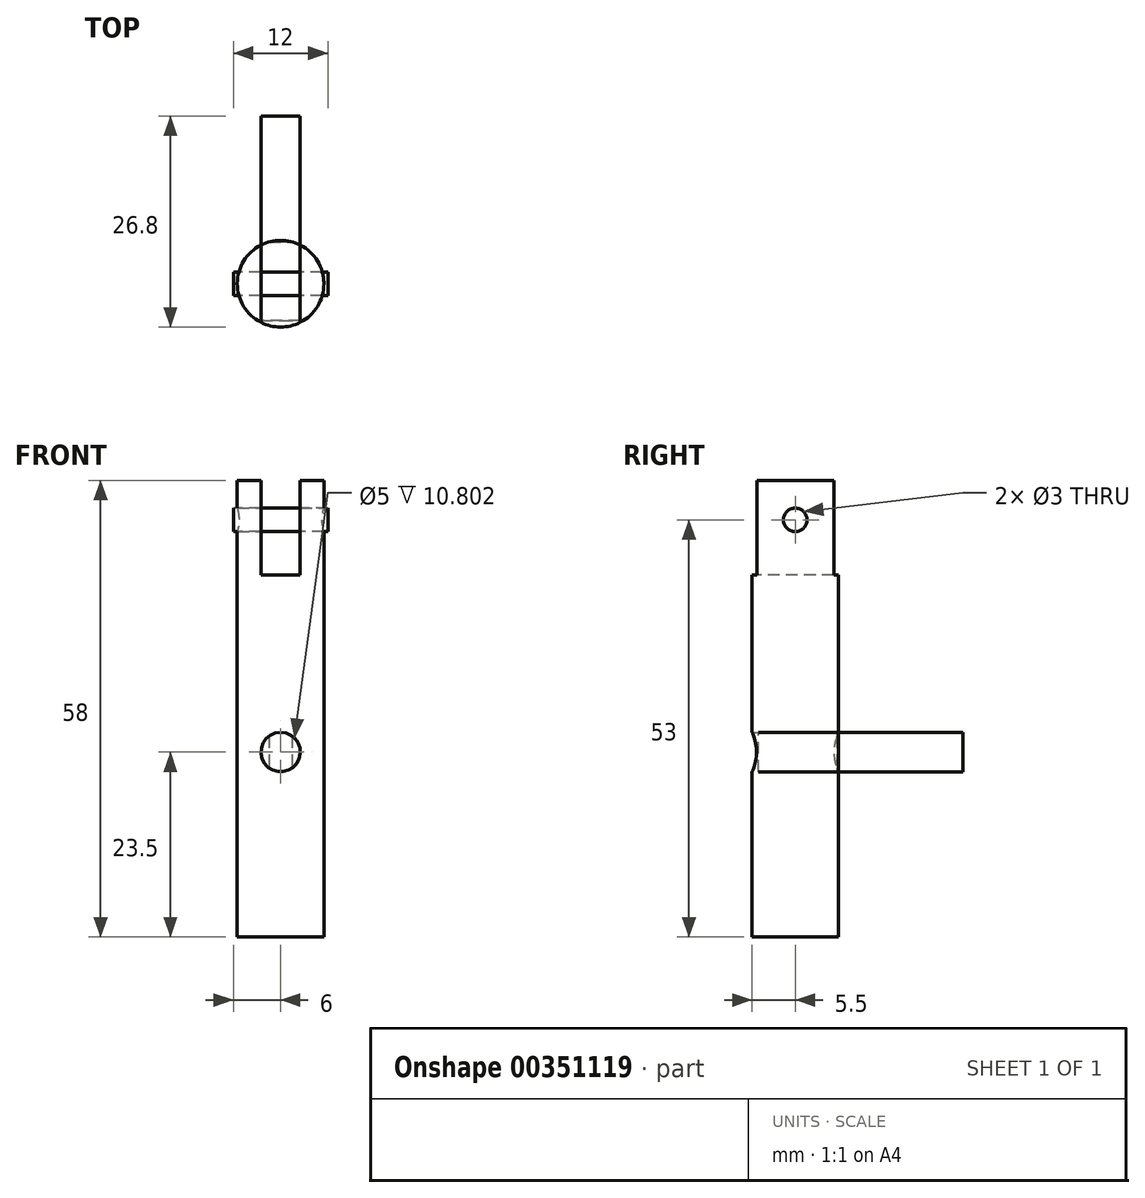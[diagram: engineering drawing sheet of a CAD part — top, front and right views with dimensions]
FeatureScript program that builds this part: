
annotation { "Feature Type Name" : "Feature", "Feature Type Description" : "" }
export const myFeature = defineFeature(function(context is Context, id is Id, definition is map)
    precondition{}
    {
        {
            var Q0;
            Q0=qCreatedBy(makeId("Top.planeOp"),FACE);
            var sketch = newSketch(context, id + "F0", { "sketchPlane" : qUnion([Q0])});
            skCircle(sketch, "E0", {"center": v(0, 0) * mm, "radius": 5.5 * mm});
            skSolve(sketch);
        }
        {
            var Q0;
            Q0=makeQuery(id+"F0.imprint","IMPRINT",FACE,{"disambiguationData":[TD([[makeQuery(id+"F0.imprint","IMPRINT",EDGE,{"derivedFrom":sQuery(id+"F0.wireOp",EDGE,"E0")}),1.0]])]});
            extrude(context, id + "F1", {"entities" : qUnion([Q0]), "depth" : 58 * mm});
        }
        {
            var Q0;
            Q0=makeQuery(id+"F1.opExtrude","CAP_FACE",FACE,{"disambiguationData":[OSD([sQuery(id+"F0.wireOp",EDGE,"E0")])],"isStart":false});
            var sketch = newSketch(context, id + "F2", { "sketchPlane" : qUnion([Q0])});
            skLineSegment(sketch, "E1", {"start": v(-2.5, 4.9) * mm, "end": v(-2.5, -4.9) * mm});
            skLineSegment(sketch, "E2", {"start": v(2.5, 4.9) * mm, "end": v(2.5, -4.9) * mm});
            skLineSegment(sketch, "E3", {"start": v(0, -1.95) * mm, "end": v(0, 2.72) * mm, "construction": true});
            skSolve(sketch);
        }
        {
            var Q0;
            {var subQ0=sQuery(id+"F2.wireOp",EDGE,"E1");Q0=makeQuery(id+"F2.imprint","IMPRINT",FACE,{"disambiguationData":[TD([[makeQuery(id+"F2.imprint","IMPRINT",EDGE,{"derivedFrom":subQ0}),1.0]])]});}
            extrude(context, id + "F3", {"entities" : qUnion([Q0]), "operationType" : NewBodyOperationType.REMOVE, "oppositeDirection" : true, "depth" : 12 * mm});
        }
        {
            var Q0;
            Q0=qCreatedBy(makeId("Right.planeOp"),FACE);
            cPlane(context, id + "F4", {"entities" : qUnion([Q0]), "cplaneType" : CPlaneType.OFFSET, "offset" : 5.5 * mm, "width" : 150 * mm, "height" : 150 * mm});
        }
        {
            var Q0;
            Q0=qCreatedBy(id+"F4.planeOp",FACE);
            var sketch = newSketch(context, id + "F5", { "sketchPlane" : qUnion([Q0])});
            skCircle(sketch, "E4", {"center": v(0, 53) * mm, "radius": 1.5 * mm});
            skSolve(sketch);
        }
        {
            var Q0;
            Q0=makeQuery(id+"F5.imprint","IMPRINT",FACE,{"disambiguationData":[TD([[makeQuery(id+"F5.imprint","IMPRINT",EDGE,{"derivedFrom":sQuery(id+"F5.wireOp",EDGE,"E4")}),1.0]])]});
            extrude(context, id + "F6", {"entities" : qUnion([Q0]), "operationType" : NewBodyOperationType.REMOVE, "endBound" : BoundingType.THROUGH_ALL, "oppositeDirection" : true, "depth" : 25 * mm});
        }
        {
            var Q0;
            Q0=makeQuery(id+"F5.imprint","IMPRINT",FACE,{"disambiguationData":[TD([[makeQuery(id+"F5.imprint","IMPRINT",EDGE,{"derivedFrom":sQuery(id+"F5.wireOp",EDGE,"E4")}),1.0]])]});
            extrude(context, id + "F7", {"entities" : qUnion([Q0]), "depth" : .5 * mm, "hasSecondDirection" : true, "secondDirectionOppositeDirection" : true, "secondDirectionDepth" : 11.5 * mm});
        }
        {
            var Q0;
            Q0=qCreatedBy(makeId("Front.planeOp"),FACE);
            cPlane(context, id + "F8", {"entities" : qUnion([Q0]), "cplaneType" : CPlaneType.OFFSET, "offset" : 5.3 * mm, "oppositeDirection" : true, "width" : 150 * mm, "height" : 150 * mm});
        }
        {
            var Q0;
            Q0=qCreatedBy(id+"F8.planeOp",FACE);
            var sketch = newSketch(context, id + "F9", { "sketchPlane" : qUnion([Q0])});
            skCircle(sketch, "E5", {"center": v(0, 23.5) * mm, "radius": 2.5 * mm});
            skSolve(sketch);
        }
        {
            var Q0;
            Q0=makeQuery(id+"F9.imprint","IMPRINT",FACE,{"disambiguationData":[TD([[makeQuery(id+"F9.imprint","IMPRINT",EDGE,{"derivedFrom":sQuery(id+"F9.wireOp",EDGE,"E5")}),1.0]])]});
            extrude(context, id + "F10", {"entities" : qUnion([Q0]), "operationType" : NewBodyOperationType.REMOVE, "endBound" : BoundingType.THROUGH_ALL, "depth" : 25 * mm});
        }
        {
            var Q0;
            Q0=makeQuery(id+"F9.imprint","IMPRINT",FACE,{"disambiguationData":[TD([[makeQuery(id+"F9.imprint","IMPRINT",EDGE,{"derivedFrom":sQuery(id+"F9.wireOp",EDGE,"E5")}),1.0]])]});
            extrude(context, id + "F11", {"entities" : qUnion([Q0]), "oppositeDirection" : true, "depth" : 16 * mm, "hasSecondDirection" : true, "secondDirectionOppositeDirection" : false, "secondDirectionDepth" : 10 * mm});
        }
    });
